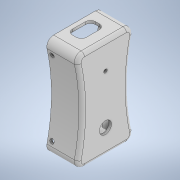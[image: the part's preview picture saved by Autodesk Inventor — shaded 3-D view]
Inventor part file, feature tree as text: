
AUTODESK INVENTOR PART (.ipt)
format: ipt  version: 2021 (Build 250183000, 183)  size: 307,200 bytes
history: native  units: mm
features: sketch x8, extrude x6, fillet x2, plane x2, mirror x2, projected_geometry x2, shell x1, other x1
ambient origin geometry x8: Origin, YZ Plane, XZ Plane, XY Plane, X Axis, Y Axis, Z Axis, Center Point
bodies: Solid1 (feature_tree)
feature tree (24):
  extrude  "Extrusion1"  Depth=27.0mm
  extrude  "Extrusion5"  Depth=2.0mm
  fillet  "Fillet1"  Radius=1.5mm
  shell  "Shell1"  Thickness=3.8mm
  extrude  "Extrusion6"  Depth=4.0mm
  extrude  "Extrusion7"  Depth=2.4mm
  fillet  "Fillet3"  Radius=17.78mm
  extrude  "Extrusion8"  Depth=6.8mm TaperAngle=0.0deg
  sketch  "Sketch13"  dims[d40=3.0mm d41=11.4mm]
  plane  "Work Plane1"
  extrude  "Extrusion13"  Depth=11.4mm
  mirror  "Mirror3"
  plane  "Work Plane2"
  mirror  "Mirror4"
  sketch  "Sketch15"  dims[d43=13.5mm d44=1.5mm d45=0.0mm d46=3.0mm d47=39.37mm d48=7.1mm d49=2.0mm d50=10.795mm d51=0.0mm d52=0.0mm d74=5.0mm d75=2.5mm d76=2.5mm d77=2.5mm d78=10.0mm d79=0.0mm]
  sketch  "Sketch1"  dims[d0=18.0mm d1=27.0mm]
  sketch  "Sketch5"  dims[d2=58.0mm d3=0.0mm d4=2.0mm d5=1.5mm d26=3.8mm]
  sketch  "Sketch6"  dims[d27=0.0mm d28=0.0mm d29=4.0mm]
  sketch  "Sketch7"  dims[d33=5.0mm d34=2.4mm d36=17.78mm]
  sketch  "Sketch8"  dims[d37=45.72mm d38=6.8mm d39=0.0mm]
  other  "Work Axis1"
  sketch  "Sketch14"  dims[d42=8.2mm]
  projected_geometry  "Project Cut Edges6"
  projected_geometry  "Project Cut Edges9"
